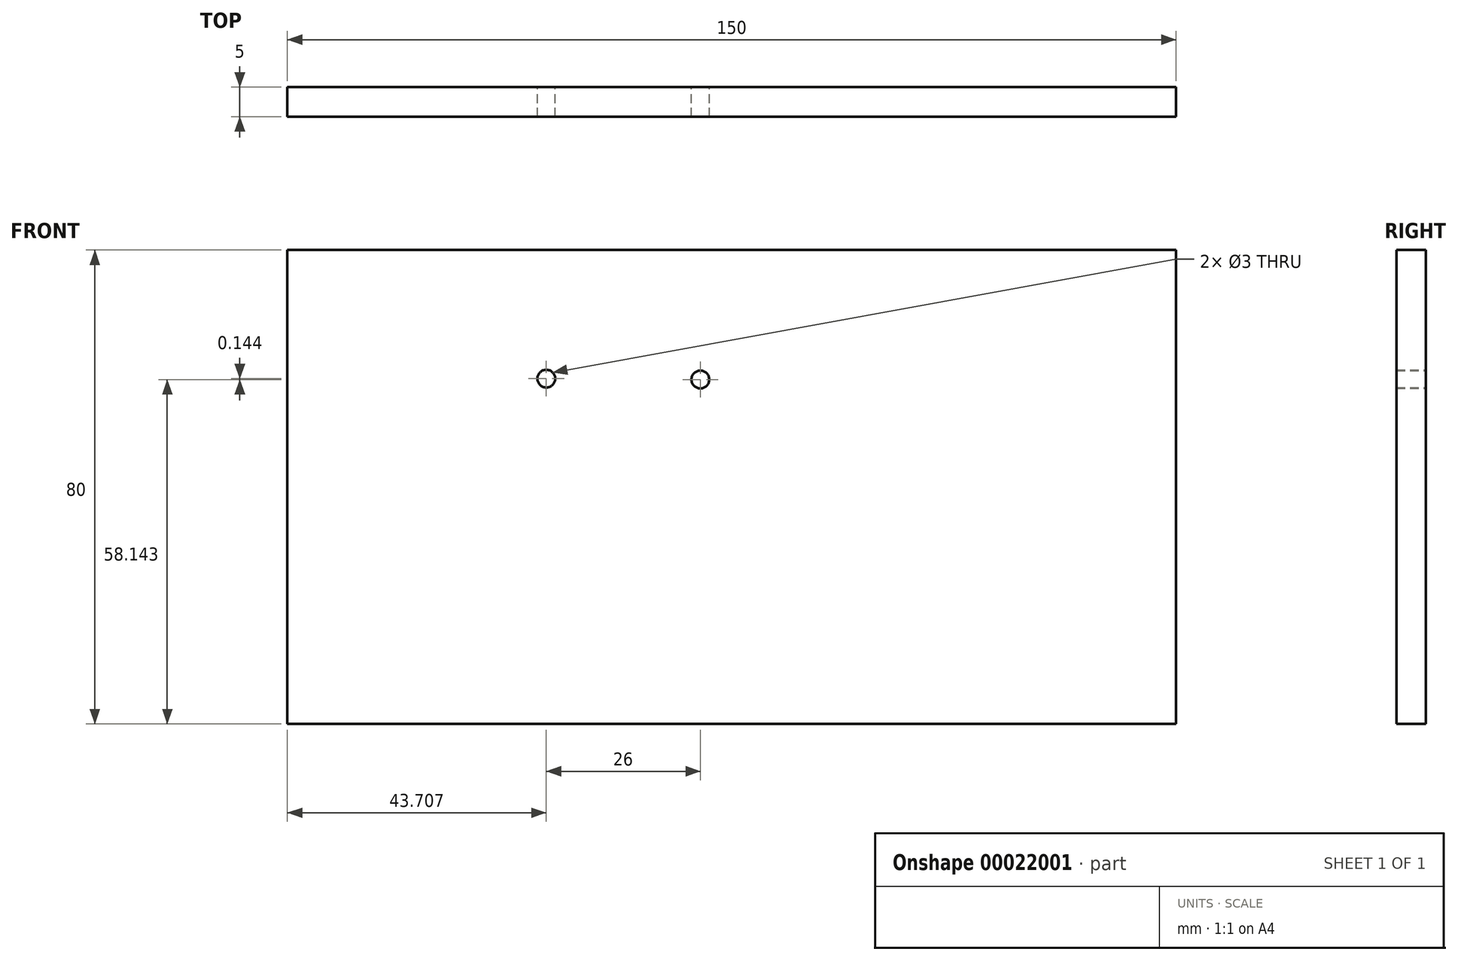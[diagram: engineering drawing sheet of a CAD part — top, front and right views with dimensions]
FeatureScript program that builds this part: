
annotation { "Feature Type Name" : "Feature", "Feature Type Description" : "" }
export const myFeature = defineFeature(function(context is Context, id is Id, definition is map)
    precondition{}
    {
        {
            var Q0;
            Q0=qCreatedBy(makeId("Front.planeOp"),FACE);
            var sketch = newSketch(context, id + "F0", { "sketchPlane" : qUnion([Q0])});
            skLineSegment(sketch, "E0.bottom", {"start": v(-76, 32.32) * mm, "end": v(74, 32.32) * mm});
            skLineSegment(sketch, "E0.top", {"start": v(-76, -47.68) * mm, "end": v(74, -47.68) * mm});
            skLineSegment(sketch, "E0.left", {"start": v(-76, 32.32) * mm, "end": v(-76, -47.68) * mm});
            skLineSegment(sketch, "E0.right", {"start": v(74, 32.32) * mm, "end": v(74, -47.68) * mm});
            skCircle(sketch, "E1", {"center": v(-32.28, 10.6) * mm, "radius": 1.5 * mm});
            skCircle(sketch, "E2", {"center": v(-6.28, 10.46) * mm, "radius": 1.5 * mm});
            skSolve(sketch);
        }
        {
            var Q0;
            Q0=makeQuery(id+"F0.imprint","IMPRINT",FACE,{"disambiguationData":[TD([[makeQuery(id+"F0.imprint","IMPRINT",EDGE,{"derivedFrom":sQuery(id+"F0.wireOp",EDGE,"E0.bottom")}),-1.0]])]});
            extrude(context, id + "F1", {"entities" : qUnion([Q0]), "depth" : 5 * mm});
        }
    });
